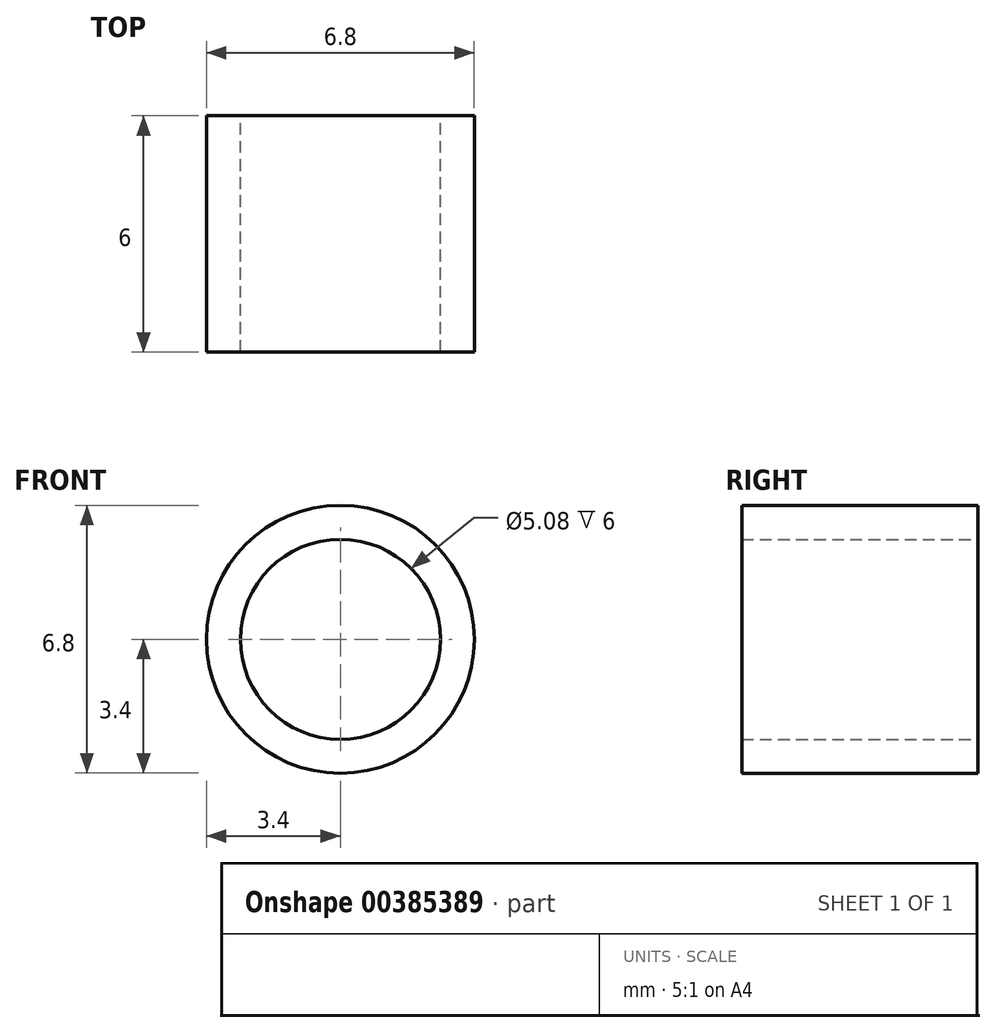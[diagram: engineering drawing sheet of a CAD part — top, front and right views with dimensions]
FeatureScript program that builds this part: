
annotation { "Feature Type Name" : "Feature", "Feature Type Description" : "" }
export const myFeature = defineFeature(function(context is Context, id is Id, definition is map)
    precondition{}
    {
        {
            var Q0;
            Q0=qCreatedBy(makeId("Front.planeOp"),FACE);
            var sketch = newSketch(context, id + "F0", { "sketchPlane" : qUnion([Q0])});
            skCircle(sketch, "E0", {"center": v(0, 0) * mm, "radius": 2.54 * mm});
            skCircle(sketch, "E1", {"center": v(0, 0) * mm, "radius": 3.4 * mm});
            skSolve(sketch);
        }
        {
            var Q0;
            Q0 = qSketchRegion(id + "F0", true);
            extrude(context, id + "F1", {"entities" : qUnion([Q0]), "depth" : 6 * mm});
        }
    });
